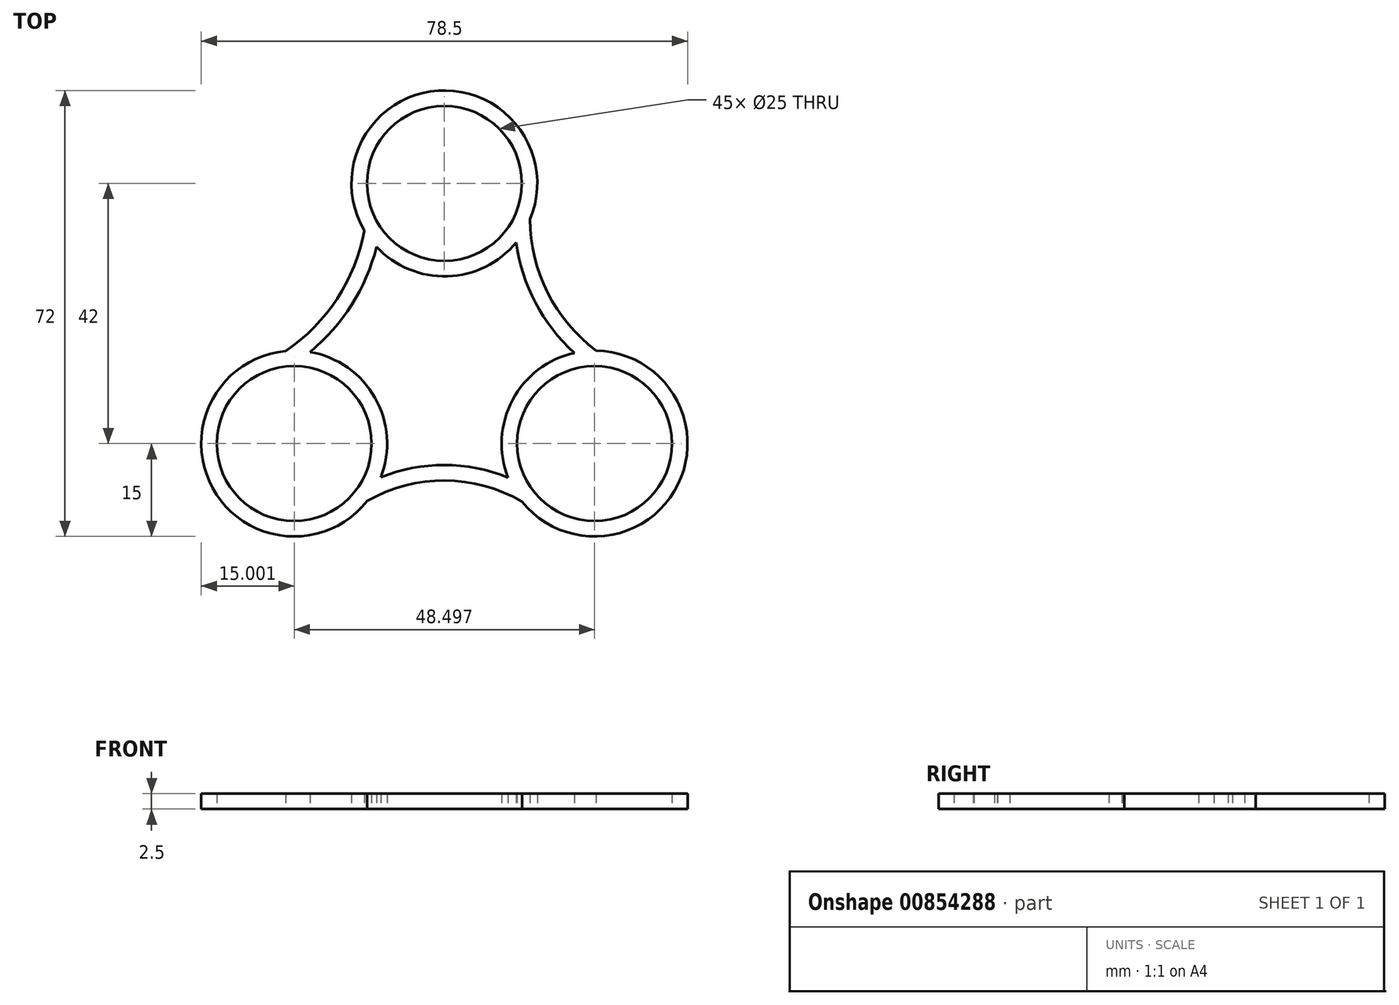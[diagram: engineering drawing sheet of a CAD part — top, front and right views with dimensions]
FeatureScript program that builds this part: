
annotation { "Feature Type Name" : "Feature", "Feature Type Description" : "" }
export const myFeature = defineFeature(function(context is Context, id is Id, definition is map)
    precondition{}
    {
        {
            var Q0;
            Q0=qCreatedBy(makeId("Top.planeOp"),FACE);
            var sketch = newSketch(context, id + "F0", { "sketchPlane" : qUnion([Q0])});
            skPoint(sketch, "E0.0.midPoint", {"position": v(0, 19.34) * mm});
            skPoint(sketch, "E1.0.midPoint", {"position": v(-15.59, -14) * mm});
            skPoint(sketch, "E2.0.midPoint", {"position": v(30.09, -20.4) * mm});
            skLineSegment(sketch, "E3", {"start": v(16.38, -9.46) * mm, "end": v(16.75, -9.67) * mm});
            skLineSegment(sketch, "E4.trimOffspring", {"start": v(-15.59, -9) * mm, "end": v(-16.75, -9.67) * mm});
            skCircle(sketch, "E5", {"center": v(24.25, -14) * mm, "radius": 12.5 * mm});
            skCircle(sketch, "E6", {"center": v(-24.25, -14) * mm, "radius": 12.5 * mm});
            skCircle(sketch, "E7", {"center": v(0, 28) * mm, "radius": 12.5 * mm});
            skCircle(sketch, "E8.0", {"center": v(-24.25, -14) * mm, "radius": 15 * mm});
            skCircle(sketch, "E9.0", {"center": v(0, 28) * mm, "radius": 15 * mm});
            skCircle(sketch, "E10.0", {"center": v(24.25, -14) * mm, "radius": 15 * mm});
            skArc(sketch, "E11", {"start": v(12.54, -23.38) * mm, "mid": v(0.06, -19.97) * mm, "end": v(-12.45, -23.26) * mm});
            skPoint(sketch, "E11.endSnap0", {"position": v(0, -23.26) * mm});
            skArc(sketch, "E12", {"start": v(-25.61, 0.94) * mm, "mid": v(-17.31, 9.4) * mm, "end": v(-12.93, 20.4) * mm});
            skArc(sketch, "E13", {"start": v(13.83, 22.2) * mm, "mid": v(16.67, 10.35) * mm, "end": v(24.48, 1) * mm});
            skArc(sketch, "E14.0", {"start": v(10.3, -19.5) * mm, "mid": v(0.02, -17.47) * mm, "end": v(-10.27, -19.44) * mm});
            skArc(sketch, "E15.0", {"start": v(11.59, 18.47) * mm, "mid": v(14.7, 8.72) * mm, "end": v(20.99, 0.64) * mm});
            skArc(sketch, "E16.0", {"start": v(-21.67, 0.78) * mm, "mid": v(-14.97, 8.42) * mm, "end": v(-10.95, 17.75) * mm});
            skSolve(sketch);
        }
        {
            var Q0;
            Q0=makeQuery(id+"F0.imprint","IMPRINT",FACE,{"disambiguationData":[TD([[makeQuery(id+"F0.imprint","IMPRINT",EDGE,{"derivedFrom":sQuery(id+"F0.wireOp",EDGE,"E6")}),-1.0]])]});
            var Q1;
            Q1=makeQuery(id+"F0.imprint","IMPRINT",FACE,{"disambiguationData":[TD([[makeQuery(id+"F0.imprint","IMPRINT",EDGE,{"derivedFrom":sQuery(id+"F0.wireOp",EDGE,"E7")}),-1.0]])]});
            var Q2;
            Q2=makeQuery(id+"F0.imprint","IMPRINT",FACE,{"disambiguationData":[TD([[makeQuery(id+"F0.imprint","IMPRINT",EDGE,{"derivedFrom":sQuery(id+"F0.wireOp",EDGE,"E5")}),-1.0]])]});
            var Q3;
            {var subQ0=sQuery(id+"F0.wireOp",EDGE,"E13");Q3=makeQuery(id+"F0.imprint","IMPRINT",FACE,{"disambiguationData":[TD([[makeQuery(id+"F0.imprint","IMPRINT",EDGE,{"derivedFrom":subQ0}),-1.0]])]});}
            var Q4;
            {var subQ0=sQuery(id+"F0.wireOp",EDGE,"E11");Q4=makeQuery(id+"F0.imprint","IMPRINT",FACE,{"disambiguationData":[TD([[makeQuery(id+"F0.imprint","IMPRINT",EDGE,{"derivedFrom":subQ0}),-1.0]])]});}
            var Q5;
            {var subQ0=sQuery(id+"F0.wireOp",EDGE,"E12");Q5=makeQuery(id+"F0.imprint","IMPRINT",FACE,{"disambiguationData":[TD([[makeQuery(id+"F0.imprint","IMPRINT",EDGE,{"derivedFrom":subQ0}),-1.0]])]});}
            extrude(context, id + "F1", {"entities" : qUnion([Q0, Q1, Q2, Q3, Q4, Q5]), "depth" : 2.5 * mm, "offsetDistance" : 25 * mm});
        }
    });
